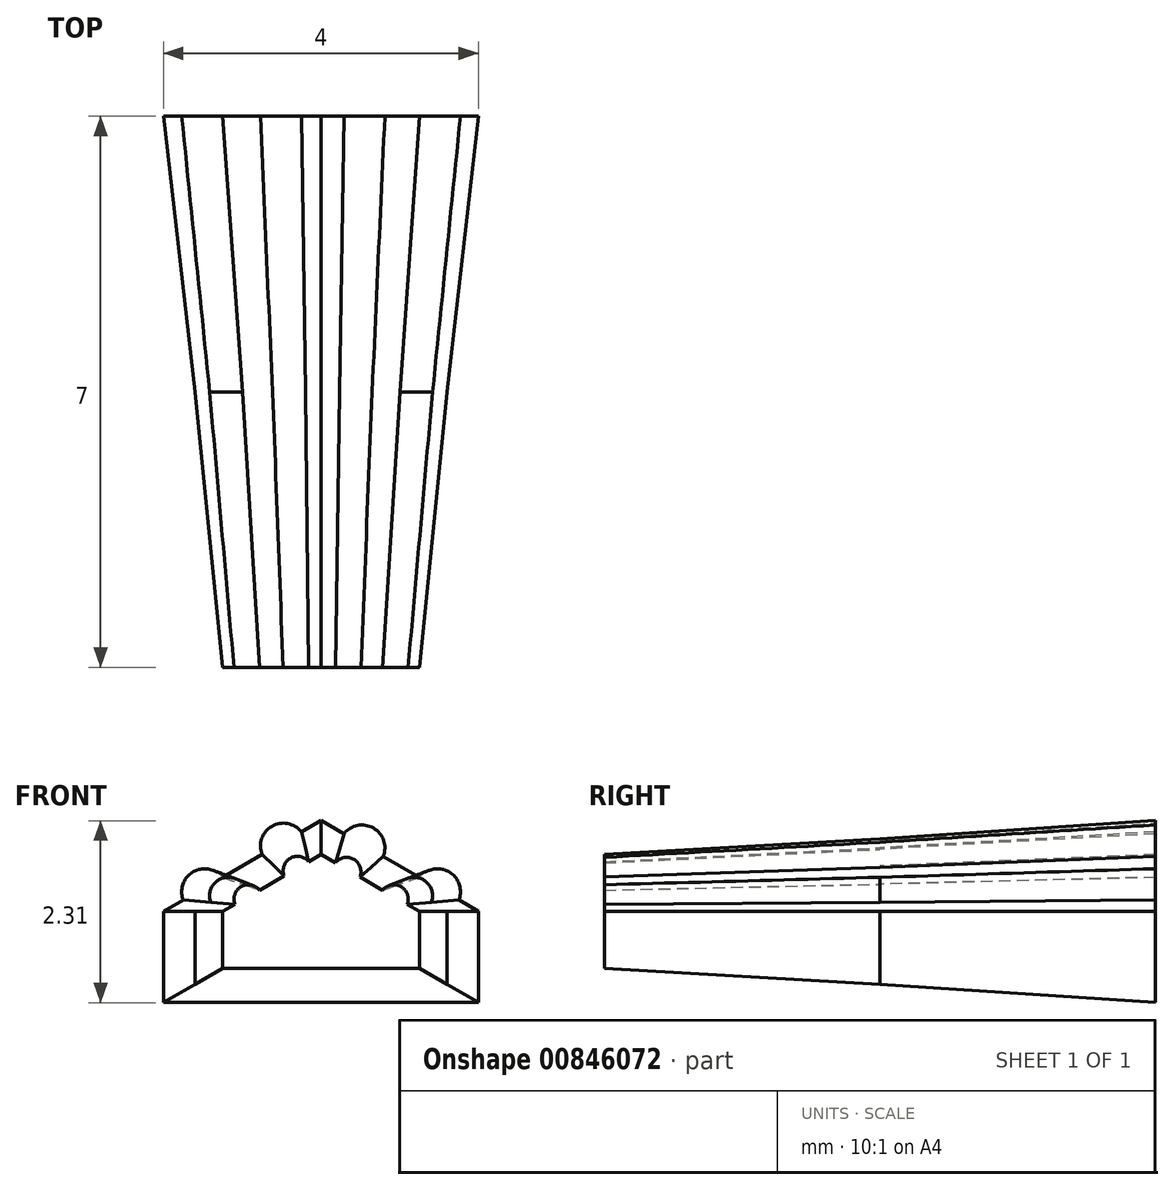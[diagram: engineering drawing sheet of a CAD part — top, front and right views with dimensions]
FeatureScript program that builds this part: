
annotation { "Feature Type Name" : "Feature", "Feature Type Description" : "" }
export const myFeature = defineFeature(function(context is Context, id is Id, definition is map)
    precondition{}
    {
        {
            var Q0;
            Q0=qCreatedBy(makeId("Front.planeOp"),FACE);
            cPlane(context, id + "F0", {"entities" : qUnion([Q0]), "cplaneType" : CPlaneType.OFFSET, "offset" : 3.5 * mm, "width" : 150 * mm, "height" : 150 * mm});
        }
        {
            var Q0;
            Q0=qCreatedBy(id+"F0.planeOp",FACE);
            cPlane(context, id + "F1", {"entities" : qUnion([Q0]), "cplaneType" : CPlaneType.OFFSET, "offset" : 3.5 * mm, "width" : 150 * mm, "height" : 150 * mm});
        }
        {
            var Q0;
            Q0=qCreatedBy(id+"F1.planeOp",FACE);
            cPlane(context, id + "F2", {"entities" : qUnion([Q0]), "cplaneType" : CPlaneType.OFFSET, "offset" : 3.5 * mm, "width" : 150 * mm, "height" : 150 * mm});
        }
        {
            var Q0;
            Q0=qCreatedBy(id+"F0.planeOp",FACE);
            var sketch = newSketch(context, id + "F3", { "sketchPlane" : qUnion([Q0])});
            skLineSegment(sketch, "E0.0", {"start": v(1.85, -0.2) * mm, "end": v(1.85, -1.36) * mm});
            skLineSegment(sketch, "E0.4", {"start": v(-2.15, -0.2) * mm, "end": v(-1.9, -0.06) * mm});
            skLineSegment(sketch, "E0.5", {"start": v(-0.15, 0.95) * mm, "end": v(0.14, 0.79) * mm});
            skPoint(sketch, "E0.0.midPoint", {"position": v(1.85, -1.36) * mm});
            skLineSegment(sketch, "E1", {"start": v(-2.15, -1.36) * mm, "end": v(-2.15, -0.2) * mm});
            skLineSegment(sketch, "E2", {"start": v(-2.15, -1.36) * mm, "end": v(1.85, -1.36) * mm});
            skArc(sketch, "E3", {"start": v(-1.4, 0.23) * mm, "mid": v(-1.77, 0.3) * mm, "end": v(-1.9, -0.06) * mm});
            skArc(sketch, "E4", {"start": v(-0.4, 0.8) * mm, "mid": v(-0.77, 0.88) * mm, "end": v(-0.9, 0.52) * mm});
            skArc(sketch, "E5", {"start": v(1.6, -0.06) * mm, "mid": v(1.48, 0.3) * mm, "end": v(1.1, 0.23) * mm});
            skArc(sketch, "E6", {"start": v(0.64, 0.5) * mm, "mid": v(0.52, 0.86) * mm, "end": v(0.14, 0.79) * mm});
            skLineSegment(sketch, "E7", {"start": v(-1.4, 0.23) * mm, "end": v(-0.9, 0.52) * mm});
            skLineSegment(sketch, "E8", {"start": v(-0.4, 0.8) * mm, "end": v(-0.15, 0.95) * mm});
            skLineSegment(sketch, "E9", {"start": v(0.64, 0.5) * mm, "end": v(1.1, 0.23) * mm});
            skLineSegment(sketch, "E10", {"start": v(1.6, -0.06) * mm, "end": v(1.85, -0.2) * mm});
            skSolve(sketch);
        }
        {
            var Q0;
            Q0=qCreatedBy(id+"F1.planeOp",FACE);
            var sketch = newSketch(context, id + "F4", { "sketchPlane" : qUnion([Q0])});
            skLineSegment(sketch, "E11.0", {"start": v(1.45, -0.2) * mm, "end": v(1.45, -1.13) * mm});
            skLineSegment(sketch, "E11.4", {"start": v(-1.75, -0.2) * mm, "end": v(-1.55, -0.09) * mm});
            skLineSegment(sketch, "E11.5", {"start": v(-0.15, 0.72) * mm, "end": v(0.08, 0.59) * mm});
            skPoint(sketch, "E11.0.midPoint", {"position": v(1.45, -1.13) * mm});
            skLineSegment(sketch, "E12", {"start": v(-1.75, -1.13) * mm, "end": v(-1.75, -0.2) * mm});
            skLineSegment(sketch, "E13", {"start": v(-1.75, -1.13) * mm, "end": v(1.45, -1.13) * mm});
            skArc(sketch, "E14", {"start": v(-1.15, 0.15) * mm, "mid": v(-1.45, 0.2) * mm, "end": v(-1.55, -0.09) * mm});
            skArc(sketch, "E15", {"start": v(-0.35, 0.6) * mm, "mid": v(-0.65, 0.66) * mm, "end": v(-0.75, 0.38) * mm});
            skArc(sketch, "E16", {"start": v(1.25, -0.09) * mm, "mid": v(1.15, 0.2) * mm, "end": v(0.85, 0.15) * mm});
            skArc(sketch, "E17", {"start": v(0.48, 0.36) * mm, "mid": v(0.38, 0.65) * mm, "end": v(0.08, 0.59) * mm});
            skLineSegment(sketch, "E18", {"start": v(-1.15, 0.15) * mm, "end": v(-0.75, 0.38) * mm});
            skLineSegment(sketch, "E19", {"start": v(-0.35, 0.6) * mm, "end": v(-0.15, 0.72) * mm});
            skLineSegment(sketch, "E20", {"start": v(0.48, 0.36) * mm, "end": v(0.85, 0.15) * mm});
            skLineSegment(sketch, "E21", {"start": v(1.25, -0.09) * mm, "end": v(1.45, -0.2) * mm});
            skSolve(sketch);
        }
        {
            var Q0;
            Q0=qCreatedBy(id+"F2.planeOp",FACE);
            var sketch = newSketch(context, id + "F5", { "sketchPlane" : qUnion([Q0])});
            skLineSegment(sketch, "E22.0", {"start": v(1.1, -0.2) * mm, "end": v(1.1, -0.92) * mm});
            skLineSegment(sketch, "E22.4", {"start": v(-1.4, -0.2) * mm, "end": v(-1.24, -0.11) * mm});
            skLineSegment(sketch, "E22.5", {"start": v(-0.15, 0.52) * mm, "end": v(0.03, 0.42) * mm});
            skPoint(sketch, "E22.0.midPoint", {"position": v(1.1, -0.92) * mm});
            skLineSegment(sketch, "E23", {"start": v(-1.4, -0.92) * mm, "end": v(-1.4, -0.2) * mm});
            skLineSegment(sketch, "E24", {"start": v(-1.4, -0.92) * mm, "end": v(1.1, -0.92) * mm});
            skArc(sketch, "E25", {"start": v(-0.93, 0.07) * mm, "mid": v(-1.16, 0.11) * mm, "end": v(-1.24, -0.11) * mm});
            skArc(sketch, "E26", {"start": v(-0.3, 0.43) * mm, "mid": v(-0.54, 0.48) * mm, "end": v(-0.62, 0.25) * mm});
            skArc(sketch, "E27", {"start": v(0.95, -0.11) * mm, "mid": v(0.87, 0.11) * mm, "end": v(0.63, 0.07) * mm});
            skArc(sketch, "E28", {"start": v(0.34, 0.24) * mm, "mid": v(0.27, 0.46) * mm, "end": v(0.03, 0.42) * mm});
            skLineSegment(sketch, "E29", {"start": v(-0.93, 0.07) * mm, "end": v(-0.62, 0.25) * mm});
            skLineSegment(sketch, "E30", {"start": v(-0.3, 0.43) * mm, "end": v(-0.15, 0.52) * mm});
            skLineSegment(sketch, "E31", {"start": v(0.34, 0.24) * mm, "end": v(0.63, 0.07) * mm});
            skLineSegment(sketch, "E32", {"start": v(0.95, -0.11) * mm, "end": v(1.1, -0.2) * mm});
            skSolve(sketch);
        }
        {
            var Q0;
            Q0=qCreatedBy(id+"F2.planeOp",FACE);
            cPlane(context, id + "F6", {"entities" : qUnion([Q0]), "cplaneType" : CPlaneType.OFFSET, "offset" : 3.5 * mm, "width" : 150 * mm, "height" : 150 * mm});
        }
        {
            var Q0;
            Q0=makeQuery(id+"F5.imprint","IMPRINT",FACE,{"disambiguationData":[TD([[makeQuery(id+"F5.imprint","IMPRINT",EDGE,{"derivedFrom":sQuery(id+"F5.wireOp",EDGE,"E22.0")}),-1.0]])]});
            var Q1;
            Q1=makeQuery(id+"F4.imprint","IMPRINT",FACE,{"disambiguationData":[TD([[makeQuery(id+"F4.imprint","IMPRINT",EDGE,{"derivedFrom":sQuery(id+"F4.wireOp",EDGE,"E11.0")}),-1.0]])]});
            loft(context, id + "F7", {"sheetProfilesArray" : [{ "sheetProfileEntities" : qUnion([Q0]) }, { "sheetProfileEntities" : qUnion([Q1]) }]});
        }
        {
            var Q1;
            Q1=makeQuery(id+"F3.imprint","IMPRINT",FACE,{"disambiguationData":[TD([[makeQuery(id+"F3.imprint","IMPRINT",EDGE,{"derivedFrom":sQuery(id+"F3.wireOp",EDGE,"E0.0")}),-1.0]])]});
            var Q2;
            Q2=makeQuery(id+"F7.opLoft","CAP_FACE",FACE,{"disambiguationData":[OSD([makeQuery(id+"F4.imprint","IMPRINT",FACE,{"disambiguationData":[TD([[makeQuery(id+"F4.imprint","IMPRINT",EDGE,{"derivedFrom":sQuery(id+"F4.wireOp",EDGE,"E11.0")}),-1.0]])]})])],"isStart":true});
            loft(context, id + "F8", {"operationType" : NewBodyOperationType.ADD, "sheetProfilesArray" : [{ "sheetProfileEntities" : qUnion([Q1]) }, { "sheetProfileEntities" : qUnion([Q2]) }]});
        }
    });
